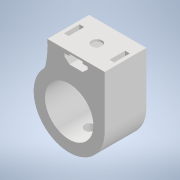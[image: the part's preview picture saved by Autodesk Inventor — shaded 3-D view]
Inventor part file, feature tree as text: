
AUTODESK INVENTOR PART (.ipt)
format: ipt  version: 2020.2 (Build 242310000, 310)  size: 197,120 bytes
history: native  units: in
note: dims shown in document units (in); Inventor stores cm internally (conversion verified against a paired STEP export)
features: extrude x5, sketch x3, plane x2, fillet x1
ambient origin geometry x8: Origin, YZ Plane, XZ Plane, XY Plane, X Axis, Y Axis, Z Axis, Center Point
bodies: Body1 (feature_tree)
feature tree (11):
  sketch  "Sketch5"  dims[d0=1.1in d1=1.0in]
  plane  "Work Plane4"
  extrude  "Extrusion7"  Depth=1.0in
  extrude  "Extrusion8"  Depth=0.175in
  extrude  "Extrusion9"  Depth=0.1in
  fillet  "Fillet1"  Radius=0.2in
  extrude  "Extrusion10"  Depth=0.1in TaperAngle=0.0deg
  plane  "Work Plane5"
  extrude  "Extrusion11"  Depth=0.1in TaperAngle=0.0deg
  sketch  "Sketch10"  dims[d2=0.93in d5=0.175in]
  sketch  "Sketch11"  dims[d6=0.45in d7=0.1in d19=0.2in d25=0.8in d26=0.0in d27=0.8in d28=0.0in d29=0.6in d30=0.0in d31=0.125in d32=0.09in d33=0.3in d34=0.1in d35=0.0in d36=0.2in d37=0.6in d38=0.0in]
